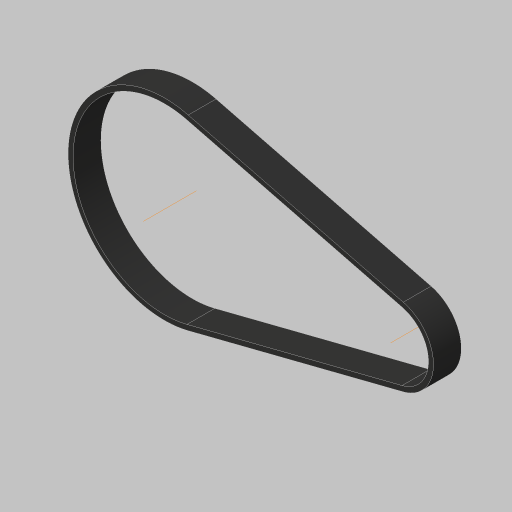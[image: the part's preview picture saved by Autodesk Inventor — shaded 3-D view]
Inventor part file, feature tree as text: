
AUTODESK INVENTOR PART (.ipt)
format: ipt  version: 2023.5 (Build 275446000, 446)  size: 167,936 bytes
history: native  units: in
note: dims shown in document units (in); Inventor stores cm internally (conversion verified against a paired STEP export)
features: sketch x3, extrude x1, other x1, projected_geometry x1
ambient origin geometry x8: Origin, YZ Plane, XZ Plane, XY Plane, X Axis, Y Axis, Z Axis, Center Point
bodies: Body1 (feature_tree)
feature tree (6):
  sketch  "Sketch2"  dims[d0=0.9023in d1=2.2558in]
  extrude  "Extrusion2"  Depth=2.2558in
  sketch  "Sketch5"  dims[d3=4.1041in d5=2.6664in d9=0.0787in d10=0.0598in d11=0.0299in d12=0.0219in d13=0.0219in d14=0.0059in d15=0.0059in d20=0.3346in d21=0.0in d22=0.0787in d23=0.0598in d24=0.0299in d25=0.0219in d26=0.0219in d27=0.0059in d28=0.0059in d29=0.0299in d30=0.0394in d31=0.0787in d32=0.0232in d34=0.0219in d35=0.0in d36=0.0in d37=0.0059in d38=0.0022in d39=0.0022in d40=0.0in d41=0.0in d42=0.0081in d43=0.0081in d44=0.0299in]
  other  "Work Axis1"
  sketch  "Sketch4"  dims[d2=1.1931in]
  projected_geometry  "Projected Loop1"
